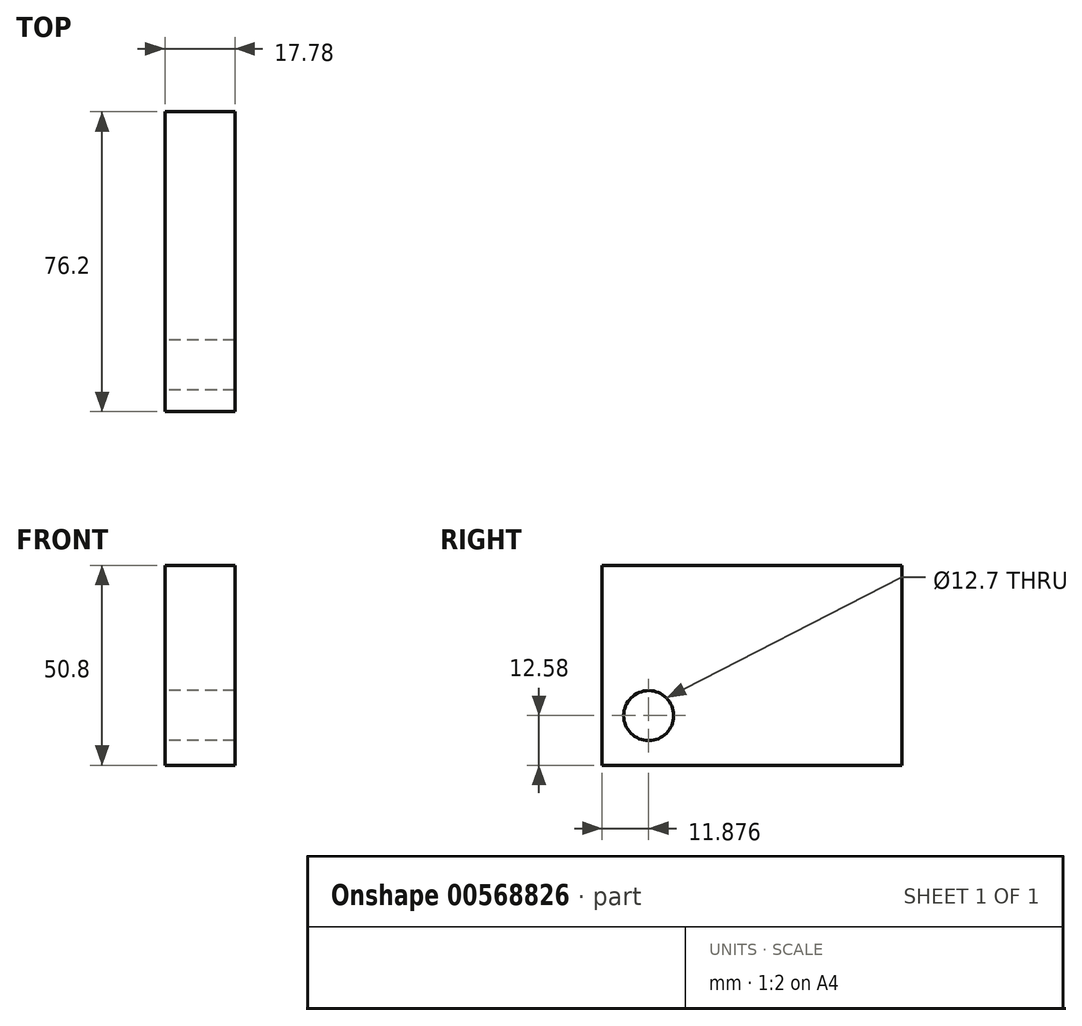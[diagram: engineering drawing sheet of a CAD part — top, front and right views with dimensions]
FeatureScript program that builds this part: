
annotation { "Feature Type Name" : "Feature", "Feature Type Description" : "" }
export const myFeature = defineFeature(function(context is Context, id is Id, definition is map)
    precondition{}
    {
        {
            var Q0;
            Q0=qCreatedBy(makeId("Right.planeOp"),FACE);
            var sketch = newSketch(context, id + "F0", { "sketchPlane" : qUnion([Q0])});
            skLineSegment(sketch, "E0.bottom", {"start": v(0, 0) * mm, "end": v(76.2, 0) * mm});
            skLineSegment(sketch, "E0.top", {"start": v(0, 50.8) * mm, "end": v(76.2, 50.8) * mm});
            skLineSegment(sketch, "E0.left", {"start": v(0, 0) * mm, "end": v(0, 50.8) * mm});
            skLineSegment(sketch, "E0.right", {"start": v(76.2, 0) * mm, "end": v(76.2, 50.8) * mm});
            skCircle(sketch, "E1", {"center": v(11.88, 12.58) * mm, "radius": 6.35 * mm});
            skSolve(sketch);
        }
        {
            var Q0;
            Q0=makeQuery(id+"F0.imprint","IMPRINT",FACE,{"disambiguationData":[TD([[makeQuery(id+"F0.imprint","IMPRINT",EDGE,{"derivedFrom":sQuery(id+"F0.wireOp",EDGE,"E0.bottom")}),1.0]])]});
            extrude(context, id + "F1", {"entities" : qUnion([Q0]), "depth" : 17.78 * mm, "offsetDistance" : 25.4 * mm});
        }
    });
